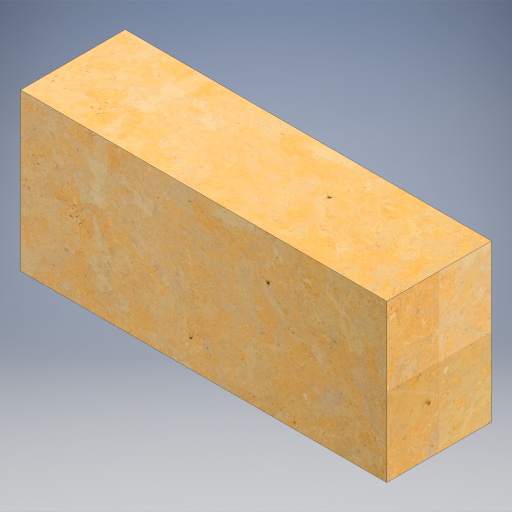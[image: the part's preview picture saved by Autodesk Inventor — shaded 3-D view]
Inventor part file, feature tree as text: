
AUTODESK INVENTOR PART (.ipt)
format: ipt  version: 2023 (Build 270158030, 158C)  size: 519,168 bytes
history: native  units: in
note: dims shown in document units (in); Inventor stores cm internally (conversion verified against a paired STEP export)
features: extrude x1, sketch x1
ambient origin geometry x8: Origin, YZ Plane, XZ Plane, XY Plane, X Axis, Y Axis, Z Axis, Center Point
bodies: Solid1 (feature_tree)
feature tree (2):
  extrude  "Extrusion1"  Depth=8.0in
  sketch  "Sketch1"  dims[d0=12.0in d1=8.0in d2=28.0in d3=0.0in]
